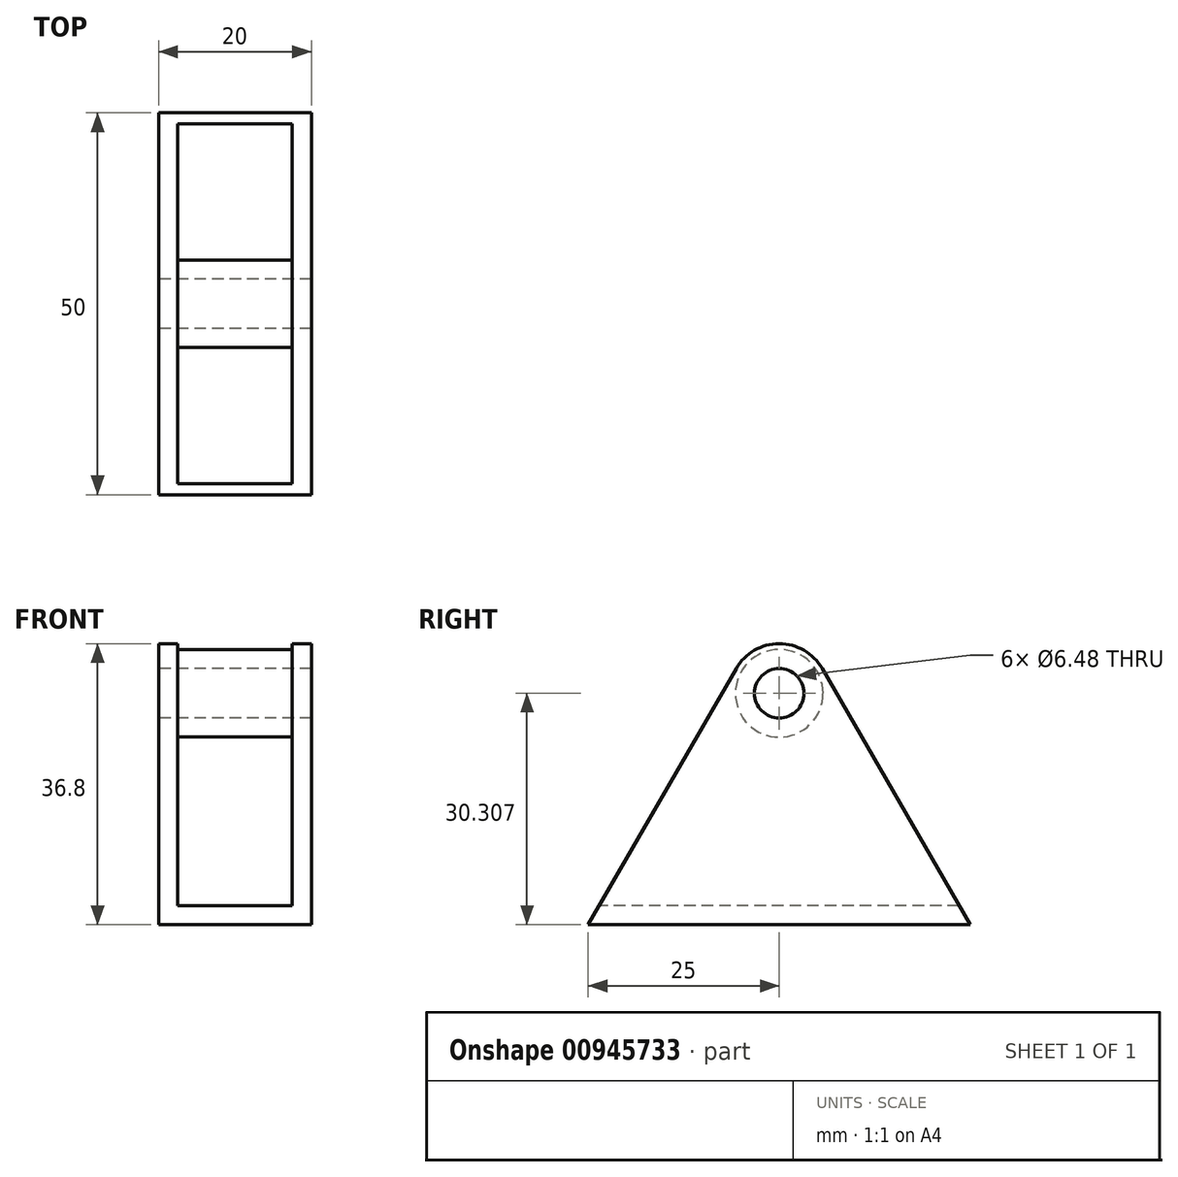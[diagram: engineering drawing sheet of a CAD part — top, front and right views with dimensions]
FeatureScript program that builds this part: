
annotation { "Feature Type Name" : "Feature", "Feature Type Description" : "" }
export const myFeature = defineFeature(function(context is Context, id is Id, definition is map)
    precondition{}
    {
        {
            var Q0;
            Q0=qCreatedBy(makeId("Right.planeOp"),FACE);
            var sketch = newSketch(context, id + "F0", { "sketchPlane" : qUnion([Q0])});
            skLineSegment(sketch, "E0", {"start": v(0, 0) * mm, "end": v(25, 0) * mm});
            skLineSegment(sketch, "E1", {"start": v(25, 0) * mm, "end": v(5.63, 33.56) * mm});
            skLineSegment(sketch, "E2.MirrorCS", {"start": v(0, 0) * mm, "end": v(-25, 0) * mm});
            skLineSegment(sketch, "E3.MirrorCS", {"start": v(-25, 0) * mm, "end": v(-5.63, 33.56) * mm});
            skArc(sketch, "E4", {"start": v(5.63, 33.56) * mm, "mid": v(0, 36.8) * mm, "end": v(-5.63, 33.56) * mm});
            skPoint(sketch, "E5.orphan", {"position": v(0, 43.3) * mm});
            skCircle(sketch, "E6", {"center": v(0, 30.3) * mm, "radius": 3.24 * mm});
            skSolve(sketch);
        }
        {
            var Q0;
            Q0=makeQuery(id+"F0.imprint","IMPRINT",FACE,{"disambiguationData":[TD([[makeQuery(id+"F0.imprint","IMPRINT",EDGE,{"derivedFrom":sQuery(id+"F0.wireOp",EDGE,"E0")}),1.0]])]});
            extrude(context, id + "F1", {"entities" : qUnion([Q0]), "endBound" : BoundingType.SYMMETRIC, "depth" : 20 * mm, "offsetDistance" : 25 * mm});
        }
        {
            var Q0;
            Q0=makeQuery(id+"F1.opExtrude","SWEPT_FACE",FACE,{"disambiguationData":[OSD([sQuery(id+"F0.wireOp",EDGE,"E1")])]});
            var Q1;
            Q1=makeQuery(id+"F1.opExtrude","SWEPT_FACE",FACE,{"disambiguationData":[OSD([sQuery(id+"F0.wireOp",EDGE,"E3.MirrorCS")])]});
            var Q2;
            Q2=makeQuery(id+"F1.opExtrude","SWEPT_FACE",FACE,{"disambiguationData":[OSD([sQuery(id+"F0.wireOp",EDGE,"E4")])]});
            shell(context, id + "F2", {"entities" : qUnion([Q0, Q1, Q2]), "thickness" : 2.5 * mm});
        }
    });
